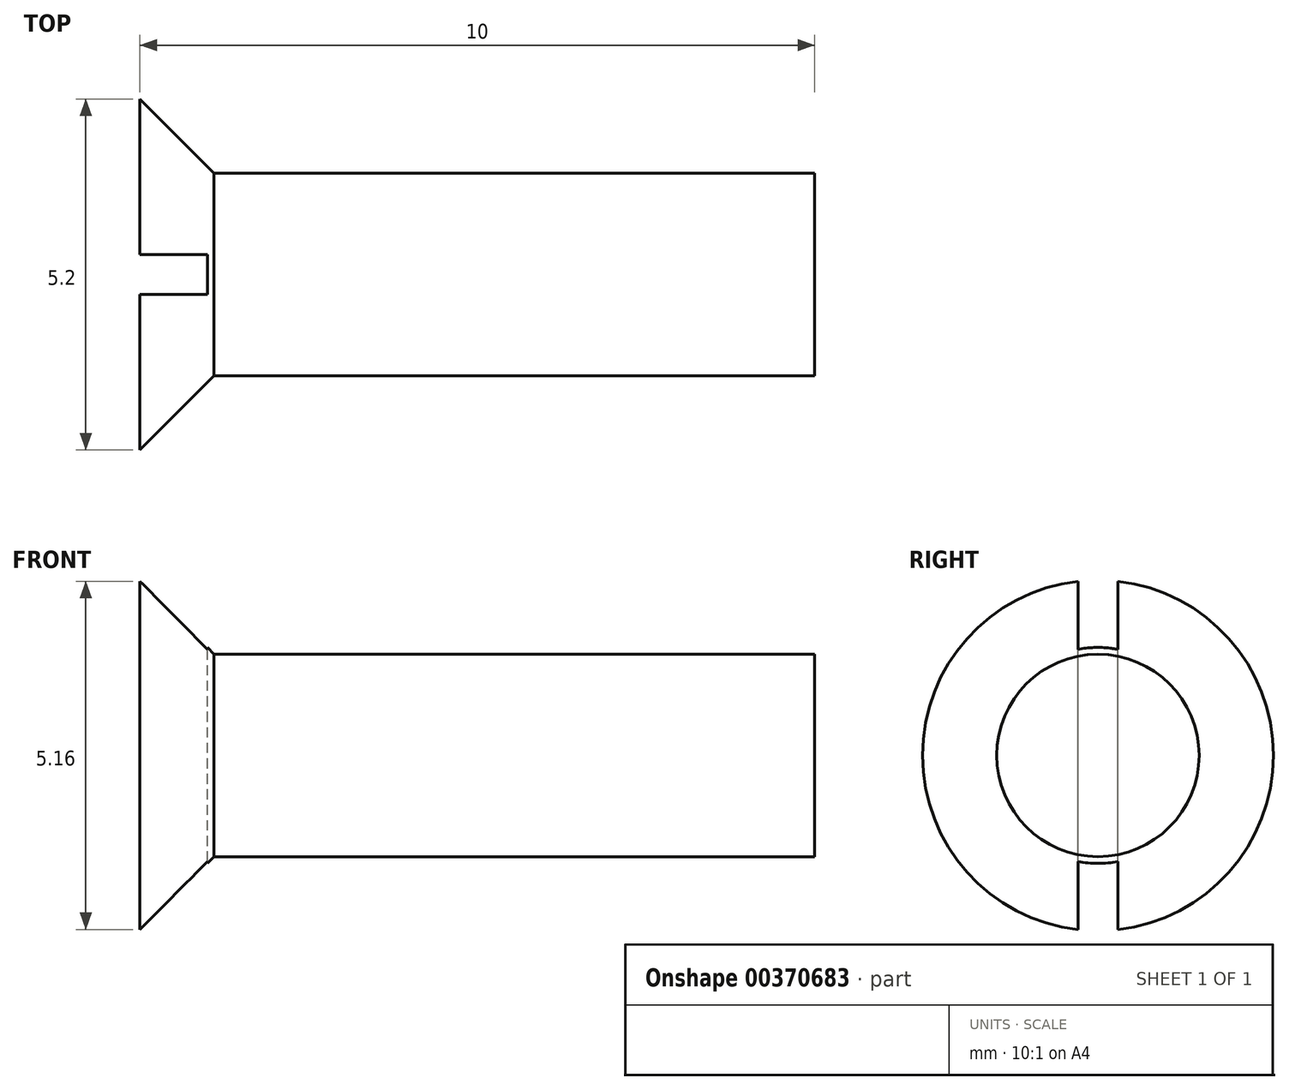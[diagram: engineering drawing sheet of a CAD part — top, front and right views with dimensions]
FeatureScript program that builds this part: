
annotation { "Feature Type Name" : "Feature", "Feature Type Description" : "" }
export const myFeature = defineFeature(function(context is Context, id is Id, definition is map)
    precondition{}
    {
        {
            var Q0;
            Q0=qCreatedBy(makeId("Front.planeOp"),FACE);
            var sketch = newSketch(context, id + "F0", { "sketchPlane" : qUnion([Q0])});
            skLineSegment(sketch, "E0", {"start": v(0, 0) * mm, "end": v(0, 2.6) * mm});
            skLineSegment(sketch, "E1", {"start": v(0, 2.6) * mm, "end": v(1.1, 1.5) * mm});
            skLineSegment(sketch, "E2", {"start": v(1.1, 1.5) * mm, "end": v(10, 1.5) * mm});
            skLineSegment(sketch, "E3", {"start": v(10, 1.5) * mm, "end": v(10, 0) * mm});
            skLineSegment(sketch, "E4", {"start": v(10, 0) * mm, "end": v(0, 0) * mm});
            skSolve(sketch);
        }
        {
            var Q0;
            Q0 = qSketchRegion(id + "F0", true);
            var Q1;
            Q1=sQuery(id+"F0.wireOp",EDGE,"E4");
            revolve(context, id + "F1", {"entities" : qUnion([Q0]), "axis" : qUnion([Q1]), "revolveType" : RevolveType.FULL});
        }
        {
            var Q0;
            Q0=makeQuery(id+"F1.opRevolve","SWEPT_FACE",FACE,{"disambiguationData":[OSD([sQuery(id+"F0.wireOp",EDGE,"E0")])]});
            var sketch = newSketch(context, id + "F2", { "sketchPlane" : qUnion([Q0])});
            skLineSegment(sketch, "E5.bottom", {"start": v(0.3, -3.04) * mm, "end": v(-0.3, -3.04) * mm});
            skLineSegment(sketch, "E5.top", {"start": v(0.3, 3.04) * mm, "end": v(-0.3, 3.04) * mm});
            skLineSegment(sketch, "E5.left", {"start": v(0.3, -3.04) * mm, "end": v(0.3, 3.04) * mm});
            skLineSegment(sketch, "E5.right", {"start": v(-0.3, -3.04) * mm, "end": v(-0.3, 3.04) * mm});
            skPoint(sketch, "E5.middle", {"position": v(0, 0) * mm});
            skSolve(sketch);
        }
        {
            var Q0;
            Q0 = qSketchRegion(id + "F2", true);
            extrude(context, id + "F3", {"entities" : qUnion([Q0]), "operationType" : NewBodyOperationType.REMOVE, "oppositeDirection" : true, "depth" : 1 * mm});
        }
    });
